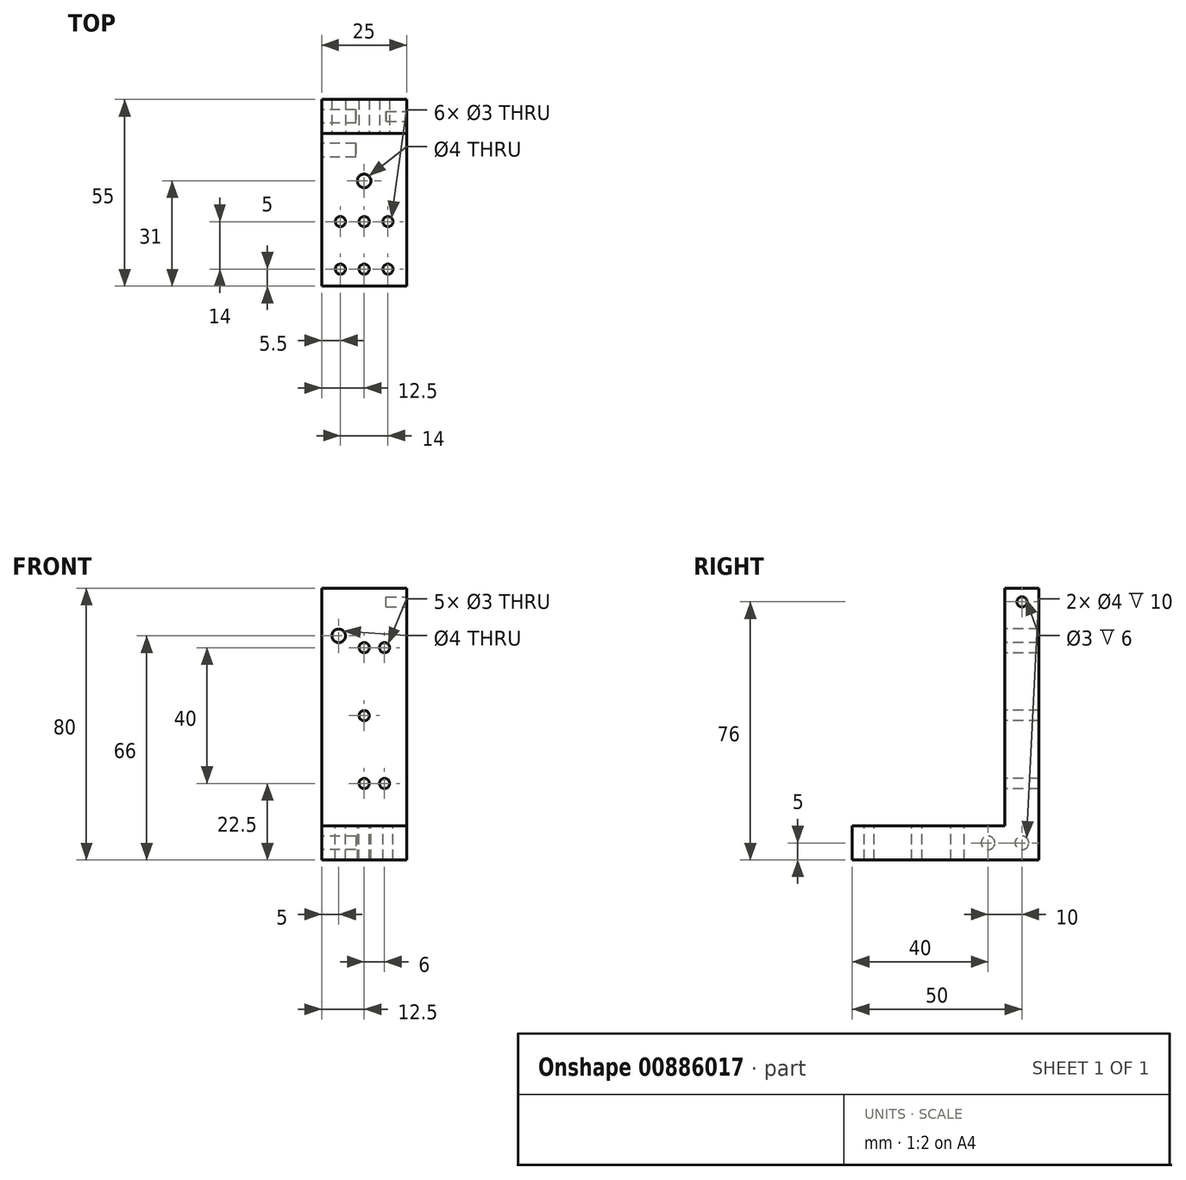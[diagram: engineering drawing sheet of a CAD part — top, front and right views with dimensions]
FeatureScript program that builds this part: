
annotation { "Feature Type Name" : "Feature", "Feature Type Description" : "" }
export const myFeature = defineFeature(function(context is Context, id is Id, definition is map)
    precondition{}
    {
        {
            var Q0;
            Q0=qCreatedBy(makeId("Front.planeOp"),FACE);
            var sketch = newSketch(context, id + "F0", { "sketchPlane" : qUnion([Q0])});
            skLineSegment(sketch, "E0.bottom", {"start": v(-12.5, 40) * mm, "end": v(12.5, 40) * mm});
            skLineSegment(sketch, "E0.top", {"start": v(-12.5, -40) * mm, "end": v(12.5, -40) * mm});
            skLineSegment(sketch, "E0.left", {"start": v(-12.5, 40) * mm, "end": v(-12.5, -40) * mm});
            skLineSegment(sketch, "E0.right", {"start": v(12.5, 40) * mm, "end": v(12.5, -40) * mm});
            skPoint(sketch, "E0.middle", {"position": v(0, 0) * mm});
            skSolve(sketch);
        }
        {
            var Q0;
            Q0=qSketchRegion(id+"F0",true);
            extrude(context, id + "F1", {"entities" : qUnion([Q0]), "depth" : 10 * mm, "offsetDistance" : 25 * mm});
        }
        {
            var Q0;
            Q0=makeQuery(id+"F1.opExtrude","CAP_FACE",FACE,{"disambiguationData":[OSD([sQuery(id+"F0.wireOp",EDGE,"E0.bottom"),sQuery(id+"F0.wireOp",EDGE,"E0.top"),sQuery(id+"F0.wireOp",EDGE,"E0.left"),sQuery(id+"F0.wireOp",EDGE,"E0.right")])],"isStart":false});
            var sketch = newSketch(context, id + "F2", { "sketchPlane" : qUnion([Q0])});
            skLineSegment(sketch, "E1.bottom", {"start": v(-12.5, -40) * mm, "end": v(12.5, -40) * mm});
            skLineSegment(sketch, "E1.top", {"start": v(-12.5, -30) * mm, "end": v(12.5, -30) * mm});
            skLineSegment(sketch, "E1.left", {"start": v(-12.5, -40) * mm, "end": v(-12.5, -30) * mm});
            skLineSegment(sketch, "E1.right", {"start": v(12.5, -40) * mm, "end": v(12.5, -30) * mm});
            skSolve(sketch);
        }
        {
            var Q0;
            Q0=qSketchRegion(id+"F2",true);
            extrude(context, id + "F3", {"entities" : qUnion([Q0]), "operationType" : NewBodyOperationType.ADD, "depth" : 45 * mm, "offsetDistance" : 25 * mm});
        }
        {
            var Q0;
            Q0=makeQuery(id+"F1.opExtrude","CAP_FACE",FACE,{"disambiguationData":[OSD([sQuery(id+"F0.wireOp",EDGE,"E0.bottom"),sQuery(id+"F0.wireOp",EDGE,"E0.top"),sQuery(id+"F0.wireOp",EDGE,"E0.left"),sQuery(id+"F0.wireOp",EDGE,"E0.right")])],"isStart":false});
            var sketch = newSketch(context, id + "F4", { "sketchPlane" : qUnion([Q0])});
            skCircle(sketch, "E2", {"center": v(-7.5, 26) * mm, "radius": 2 * mm});
            skCircle(sketch, "E3", {"center": v(0, -17.5) * mm, "radius": 1.5 * mm});
            skCircle(sketch, "E4", {"center": v(0, 2.5) * mm, "radius": 1.5 * mm});
            skCircle(sketch, "E5", {"center": v(0, 22.5) * mm, "radius": 1.5 * mm});
            skCircle(sketch, "E6", {"center": v(6, 22.5) * mm, "radius": 1.5 * mm});
            skCircle(sketch, "E7", {"center": v(6, -17.5) * mm, "radius": 1.5 * mm});
            skSolve(sketch);
        }
        {
            var Q0;
            Q0 = qSketchRegion(id + "F4", true);
            extrude(context, id + "F5", {"entities" : qUnion([Q0]), "operationType" : NewBodyOperationType.REMOVE, "endBound" : BoundingType.THROUGH_ALL, "oppositeDirection" : true, "depth" : 25 * mm, "offsetDistance" : 25 * mm});
        }
        {
            var Q0;
            Q0=makeQuery(id+"F3.boolean.opBoolean","MERGE",FACE,{"derivedFrom":[makeQuery(id+"F1.opExtrude","SWEPT_FACE",FACE,{"disambiguationData":[OSD([sQuery(id+"F0.wireOp",EDGE,"E0.right")])]}),makeQuery(id+"F3.opExtrude","SWEPT_FACE",FACE,{"disambiguationData":[OSD([sQuery(id+"F2.wireOp",EDGE,"E1.right")])]})]});
            var sketch = newSketch(context, id + "F6", { "sketchPlane" : qUnion([Q0])});
            skCircle(sketch, "E8", {"center": v(-5, 36) * mm, "radius": 1.5 * mm});
            skSolve(sketch);
        }
        {
            var Q0;
            Q0 = qSketchRegion(id + "F6", true);
            extrude(context, id + "F7", {"entities" : qUnion([Q0]), "operationType" : NewBodyOperationType.REMOVE, "oppositeDirection" : true, "depth" : 6 * mm, "offsetDistance" : 25 * mm});
        }
        {
            var Q0;
            Q0=makeQuery(id+"F3.opExtrude","SWEPT_FACE",FACE,{"disambiguationData":[OSD([sQuery(id+"F2.wireOp",EDGE,"E1.top")])]});
            var sketch = newSketch(context, id + "F8", { "sketchPlane" : qUnion([Q0])});
            skCircle(sketch, "E9", {"center": v(0, -36) * mm, "radius": 1.5 * mm});
            skPoint(sketch, "E10", {"position": v(0, -10) * mm});
            skCircle(sketch, "E11", {"center": v(0, -24) * mm, "radius": 2 * mm});
            skCircle(sketch, "E12", {"center": v(-7, -36) * mm, "radius": 1.5 * mm});
            skCircle(sketch, "E13", {"center": v(7, -36) * mm, "radius": 1.5 * mm});
            skCircle(sketch, "E14", {"center": v(0, -50) * mm, "radius": 1.5 * mm});
            skCircle(sketch, "E15", {"center": v(-7, -50) * mm, "radius": 1.5 * mm});
            skCircle(sketch, "E16", {"center": v(7, -50) * mm, "radius": 1.5 * mm});
            skSolve(sketch);
        }
        {
            var Q0;
            Q0 = qSketchRegion(id + "F8", true);
            extrude(context, id + "F9", {"entities" : qUnion([Q0]), "operationType" : NewBodyOperationType.REMOVE, "endBound" : BoundingType.THROUGH_ALL, "oppositeDirection" : true, "depth" : 25 * mm, "offsetDistance" : 25 * mm});
        }
        {
            var Q0;
            Q0=makeQuery(id+"F3.boolean.opBoolean","MERGE",FACE,{"derivedFrom":[makeQuery(id+"F1.opExtrude","SWEPT_FACE",FACE,{"disambiguationData":[OSD([sQuery(id+"F0.wireOp",EDGE,"E0.left")])]}),makeQuery(id+"F3.opExtrude","SWEPT_FACE",FACE,{"disambiguationData":[OSD([sQuery(id+"F2.wireOp",EDGE,"E1.left")])]})]});
            var sketch = newSketch(context, id + "F10", { "sketchPlane" : qUnion([Q0])});
            skCircle(sketch, "E17", {"center": v(5, -35) * mm, "radius": 2 * mm});
            skCircle(sketch, "E18", {"center": v(15, -35) * mm, "radius": 2 * mm});
            skSolve(sketch);
        }
        {
            var Q0;
            Q0 = qSketchRegion(id + "F10", true);
            extrude(context, id + "F11", {"entities" : qUnion([Q0]), "operationType" : NewBodyOperationType.REMOVE, "oppositeDirection" : true, "depth" : 10 * mm, "offsetDistance" : 25 * mm});
        }
    });
